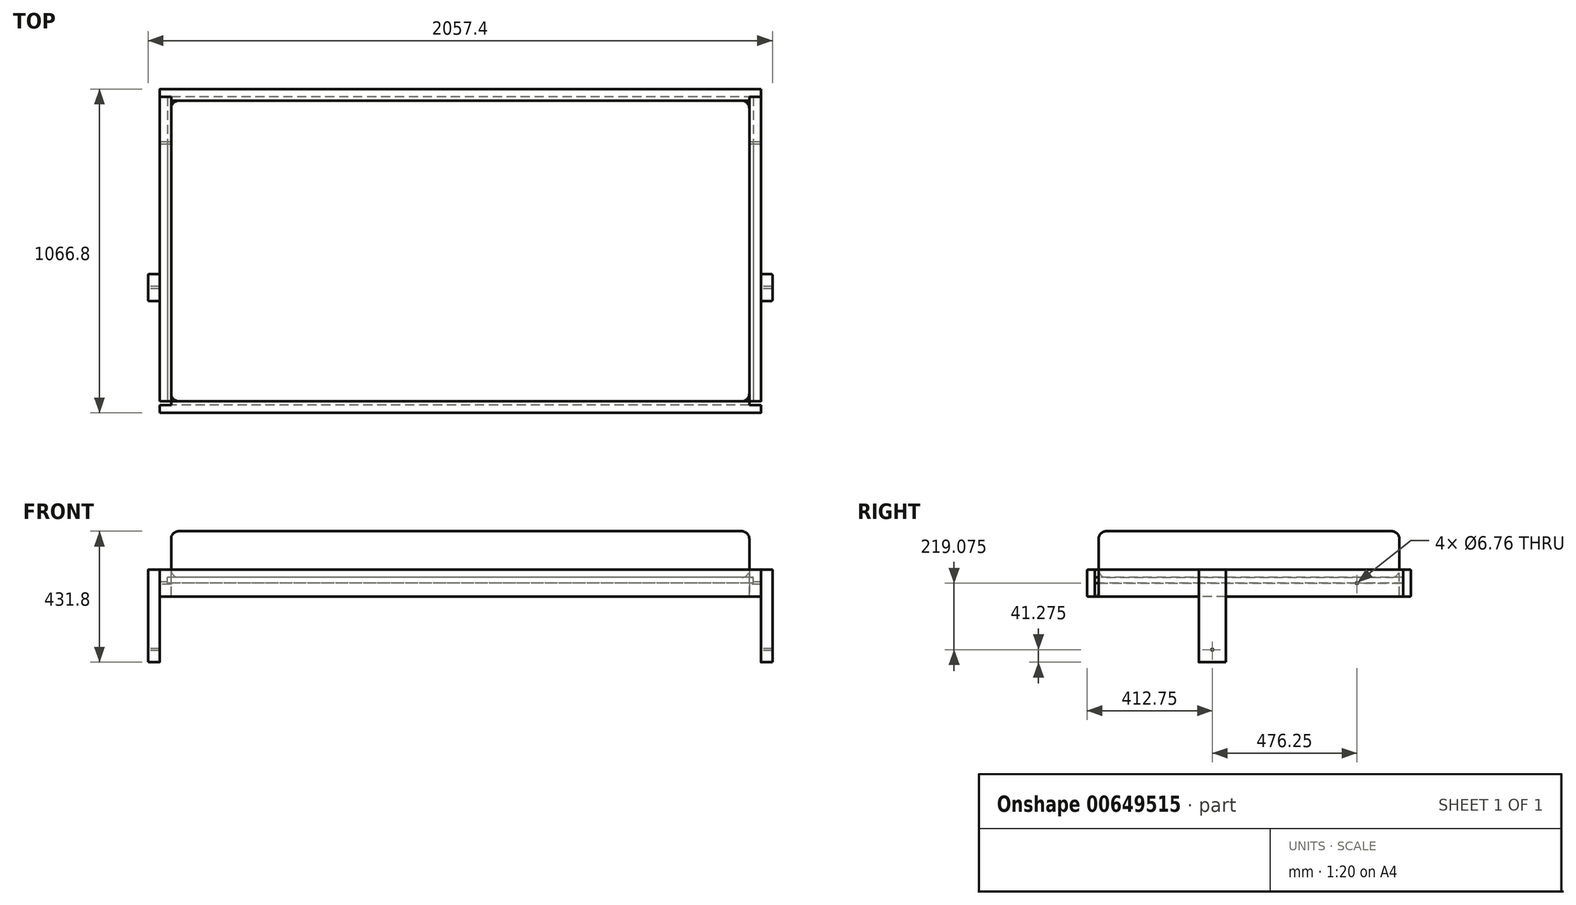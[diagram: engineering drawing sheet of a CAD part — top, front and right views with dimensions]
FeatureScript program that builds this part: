
annotation { "Feature Type Name" : "Feature", "Feature Type Description" : "" }
export const myFeature = defineFeature(function(context is Context, id is Id, definition is map)
    precondition{}
    {
        {
            var Q0;
            Q0=qCreatedBy(makeId("Top.planeOp"),FACE);
            var sketch = newSketch(context, id + "F0", { "sketchPlane" : qUnion([Q0])});
            skLineSegment(sketch, "E0.bottom", {"start": v(965.2, -508) * mm, "end": v(-965.2, -508) * mm});
            skLineSegment(sketch, "E0.top", {"start": v(965.2, 508) * mm, "end": v(-965.2, 508) * mm});
            skLineSegment(sketch, "E0.left", {"start": v(965.2, -508) * mm, "end": v(965.2, 508) * mm});
            skLineSegment(sketch, "E0.right", {"start": v(-965.2, -508) * mm, "end": v(-965.2, 508) * mm});
            skPoint(sketch, "E0.middle", {"position": v(0, 0) * mm});
            skLineSegment(sketch, "E1.0", {"start": v(952.5, 495.3) * mm, "end": v(-952.5, 495.3) * mm});
            skLineSegment(sketch, "E1.1", {"start": v(952.5, -495.3) * mm, "end": v(952.5, 495.3) * mm});
            skLineSegment(sketch, "E1.2", {"start": v(952.5, -495.3) * mm, "end": v(-952.5, -495.3) * mm});
            skLineSegment(sketch, "E1.3", {"start": v(-952.5, -495.3) * mm, "end": v(-952.5, 495.3) * mm});
            skLineSegment(sketch, "E2.0", {"start": v(990.6, 533.4) * mm, "end": v(-990.6, 533.4) * mm});
            skLineSegment(sketch, "E2.1", {"start": v(990.6, -533.4) * mm, "end": v(990.6, 533.4) * mm});
            skLineSegment(sketch, "E2.2", {"start": v(990.6, -533.4) * mm, "end": v(-990.6, -533.4) * mm});
            skLineSegment(sketch, "E2.3", {"start": v(-990.6, -533.4) * mm, "end": v(-990.6, 533.4) * mm});
            skSolve(sketch);
        }
        {
            var Q0;
            Q0=makeQuery(id+"F0.imprint","IMPRINT",FACE,{"disambiguationData":[TD([[makeQuery(id+"F0.imprint","IMPRINT",EDGE,{"derivedFrom":sQuery(id+"F0.wireOp",EDGE,"E1.0")}),1.0]])]});
            extrude(context, id + "F1", {"entities" : qUnion([Q0]), "depth" : 152.4 * mm, "offsetDistance" : 25.4 * mm});
        }
        {
            var Q0;
            Q0=makeQuery(id+"F1.opExtrude","CAP_FACE",FACE,{"disambiguationData":[OSD([sQuery(id+"F0.wireOp",EDGE,"E1.0"),sQuery(id+"F0.wireOp",EDGE,"E1.1"),sQuery(id+"F0.wireOp",EDGE,"E1.2"),sQuery(id+"F0.wireOp",EDGE,"E1.3")])],"isStart":false});
            var Q1;
            Q1=makeQuery(id+"F1.opExtrude","SWEPT_FACE",FACE,{"disambiguationData":[OSD([sQuery(id+"F0.wireOp",EDGE,"E1.3")])]});
            var Q2;
            Q2=makeQuery(id+"F1.opExtrude","SWEPT_FACE",FACE,{"disambiguationData":[OSD([sQuery(id+"F0.wireOp",EDGE,"E1.2")])]});
            var Q3;
            Q3=makeQuery(id+"F1.opExtrude","SWEPT_FACE",FACE,{"disambiguationData":[OSD([sQuery(id+"F0.wireOp",EDGE,"E1.1")])]});
            var Q4;
            Q4=makeQuery(id+"F1.opExtrude","SWEPT_FACE",FACE,{"disambiguationData":[OSD([sQuery(id+"F0.wireOp",EDGE,"E1.0")])]});
            fillet(context, id + "F2", {"entities" : qUnion([Q0, Q1, Q2, Q3, Q4]), "radius" : 25.4 * mm, "tangentPropagation" : true, "allowEdgeOverflow" : false});
        }
        {
            var Q0;
            Q0=makeQuery(id+"F0.imprint","IMPRINT",FACE,{"disambiguationData":[TD([[makeQuery(id+"F0.imprint","IMPRINT",EDGE,{"derivedFrom":sQuery(id+"F0.wireOp",EDGE,"E1.0")}),1.0]])]});
            var Q1;
            Q1=makeQuery(id+"F0.imprint","IMPRINT",FACE,{"disambiguationData":[TD([[makeQuery(id+"F0.imprint","IMPRINT",EDGE,{"derivedFrom":sQuery(id+"F0.wireOp",EDGE,"E0.bottom")}),-1.0]])]});
            extrude(context, id + "F3", {"entities" : qUnion([Q0, Q1]), "oppositeDirection" : true, "depth" : 19.05 * mm, "offsetDistance" : 25.4 * mm});
        }
        {
            var Q0;
            Q0=makeQuery(id+"F3.opExtrude","SWEPT_FACE",FACE,{"disambiguationData":[OSD([sQuery(id+"F0.wireOp",EDGE,"E0.bottom")])]});
            var sketch = newSketch(context, id + "F4", { "sketchPlane" : qUnion([Q0])});
            skLineSegment(sketch, "E3.bottom", {"start": v(-955.68, 25.4) * mm, "end": v(-987.43, 25.4) * mm});
            skLineSegment(sketch, "E3.top", {"start": v(-955.68, -63.5) * mm, "end": v(-987.43, -63.5) * mm});
            skLineSegment(sketch, "E3.left", {"start": v(-952.5, 22.23) * mm, "end": v(-952.5, -60.33) * mm});
            skLineSegment(sketch, "E3.right", {"start": v(-990.6, 22.23) * mm, "end": v(-990.6, -60.33) * mm});
            skPoint(sketch, "E3.middle", {"position": v(-971.55, -19.05) * mm});
            skPoint(sketch, "E4.visualSharp", {"position": v(-990.6, 25.4) * mm});
            skArc(sketch, "E4.filletArc", {"start": v(-987.43, 25.4) * mm, "mid": v(-989.67, 24.47) * mm, "end": v(-990.6, 22.23) * mm});
            skPoint(sketch, "E5.visualSharp", {"position": v(-952.5, 25.4) * mm});
            skArc(sketch, "E5.filletArc", {"start": v(-952.5, 22.23) * mm, "mid": v(-953.43, 24.47) * mm, "end": v(-955.68, 25.4) * mm});
            skPoint(sketch, "E6.visualSharp", {"position": v(-952.5, -63.5) * mm});
            skArc(sketch, "E6.filletArc", {"start": v(-955.68, -63.5) * mm, "mid": v(-953.43, -62.57) * mm, "end": v(-952.5, -60.33) * mm});
            skPoint(sketch, "E7.visualSharp", {"position": v(-990.6, -63.5) * mm});
            skArc(sketch, "E7.filletArc", {"start": v(-990.6, -60.33) * mm, "mid": v(-989.67, -62.57) * mm, "end": v(-987.43, -63.5) * mm});
            skSolve(sketch);
        }
        {
            var Q0;
            {var subQ5=sQuery(id+"F4.wireOp",EDGE,"E3.bottom");Q0=makeQuery(id+"F4.imprint","IMPRINT",FACE,{"disambiguationData":[TD([[makeQuery(id+"F4.imprint","IMPRINT",EDGE,{"derivedFrom":subQ5}),1.0]])]});}
            var Q1;
            Q1=makeQuery(id+"F3.opExtrude","SWEPT_FACE",FACE,{"disambiguationData":[OSD([sQuery(id+"F0.wireOp",EDGE,"E0.top")])]});
            extrude(context, id + "F5", {"entities" : qUnion([Q0]), "endBound" : BoundingType.UP_TO_SURFACE, "oppositeDirection" : true, "depth" : 25.4 * mm, "endBoundEntityFace" : qUnion([Q1]), "offsetDistance" : 25.4 * mm});
        }
        {
            var Q0;
            Q0=makeQuery(id+"F5.opExtrude","SWEPT_BODY",BODY,{"disambiguationData":[OSD([sQuery(id+"F0.wireOp",EDGE,"E0.bottom"),sQuery(id+"F0.wireOp",EDGE,"E0.right"),sQuery(id+"F4.wireOp",EDGE,"E3.bottom"),sQuery(id+"F4.wireOp",EDGE,"E3.top"),sQuery(id+"F4.wireOp",EDGE,"E3.left"),sQuery(id+"F4.wireOp",EDGE,"E3.right"),sQuery(id+"F4.wireOp",EDGE,"E4.filletArc"),sQuery(id+"F4.wireOp",EDGE,"E5.filletArc"),sQuery(id+"F4.wireOp",EDGE,"E6.filletArc"),sQuery(id+"F4.wireOp",EDGE,"E7.filletArc")])]});
            var Q1;
            Q1=qCreatedBy(makeId("Right.planeOp"),FACE);
            mirror(context, id + "F6", {"entities" : qUnion([Q0]), "mirrorPlane" : qUnion([Q1])});
        }
        {
            var Q0;
            Q0=makeQuery(id+"F5.opExtrude","SWEPT_FACE",FACE,{"disambiguationData":[OSD([sQuery(id+"F4.wireOp",EDGE,"E3.right")])]});
            var sketch = newSketch(context, id + "F7", { "sketchPlane" : qUnion([Q0])});
            skLineSegment(sketch, "E8.bottom", {"start": v(530.23, -63.5) * mm, "end": v(498.48, -63.5) * mm});
            skLineSegment(sketch, "E8.top", {"start": v(530.23, 25.4) * mm, "end": v(498.48, 25.4) * mm});
            skLineSegment(sketch, "E8.left", {"start": v(533.4, -60.33) * mm, "end": v(533.4, 22.22) * mm});
            skLineSegment(sketch, "E8.right", {"start": v(495.3, -60.33) * mm, "end": v(495.3, 22.22) * mm});
            skPoint(sketch, "E8.middle", {"position": v(514.35, -19.05) * mm});
            skPoint(sketch, "E9.visualSharp", {"position": v(495.3, 25.4) * mm});
            skArc(sketch, "E9.filletArc", {"start": v(498.48, 25.4) * mm, "mid": v(496.23, 24.47) * mm, "end": v(495.3, 22.22) * mm});
            skPoint(sketch, "E10.visualSharp", {"position": v(533.4, 25.4) * mm});
            skArc(sketch, "E10.filletArc", {"start": v(533.4, 22.22) * mm, "mid": v(532.47, 24.47) * mm, "end": v(530.23, 25.4) * mm});
            skPoint(sketch, "E11.visualSharp", {"position": v(533.4, -63.5) * mm});
            skArc(sketch, "E11.filletArc", {"start": v(530.23, -63.5) * mm, "mid": v(532.47, -62.57) * mm, "end": v(533.4, -60.33) * mm});
            skPoint(sketch, "E12.visualSharp", {"position": v(495.3, -63.5) * mm});
            skArc(sketch, "E12.filletArc", {"start": v(495.3, -60.33) * mm, "mid": v(496.23, -62.57) * mm, "end": v(498.48, -63.5) * mm});
            skSolve(sketch);
        }
        {
            var Q0;
            Q0 = qSketchRegion(id + "F7", true);
            var Q1;
            Q1=makeQuery(id+"F6.opPattern","COPY",FACE,{"derivedFrom":makeQuery(id+"F5.opExtrude","SWEPT_FACE",FACE,{"disambiguationData":[OSD([sQuery(id+"F4.wireOp",EDGE,"E3.right")])]}),"instanceName":"1"});
            extrude(context, id + "F8", {"entities" : qUnion([Q0]), "endBound" : BoundingType.UP_TO_SURFACE, "oppositeDirection" : true, "depth" : 25.4 * mm, "endBoundEntityFace" : qUnion([Q1]), "offsetDistance" : 25.4 * mm});
        }
        {
            var Q0;
            Q0=makeQuery(id+"F8.opExtrude","SWEPT_FACE",FACE,{"disambiguationData":[OSD([sQuery(id+"F7.wireOp",EDGE,"E8.top")])]});
            var sketch = newSketch(context, id + "F9", { "sketchPlane" : qUnion([Q0])});
            skLineSegment(sketch, "E13.0", {"start": v(-990.6, 508) * mm, "end": v(-990.6, -508) * mm});
            skLineSegment(sketch, "E13.2", {"start": v(-952.5, 508) * mm, "end": v(-952.5, -508) * mm});
            skLineSegment(sketch, "E14", {"start": v(-952.5, -508) * mm, "end": v(-990.6, -508) * mm});
            skLineSegment(sketch, "E15.0", {"start": v(990.6, -495.3) * mm, "end": v(-990.6, -495.3) * mm});
            skLineSegment(sketch, "E16.0", {"start": v(990.6, 508) * mm, "end": v(990.6, -508) * mm});
            skLineSegment(sketch, "E17.0", {"start": v(952.5, 508) * mm, "end": v(952.5, -508) * mm});
            skLineSegment(sketch, "E18", {"start": v(952.5, -508) * mm, "end": v(990.6, -508) * mm});
            skSolve(sketch);
        }
        {
            var Q0;
            Q0 = qSketchRegion(id + "F9", true);
            extrude(context, id + "F10", {"entities" : qUnion([Q0]), "operationType" : NewBodyOperationType.REMOVE, "endBound" : BoundingType.THROUGH_ALL, "oppositeDirection" : true, "depth" : 25.4 * mm, "offsetDistance" : 25.4 * mm});
        }
        {
            var Q0;
            Q0=makeQuery(id+"F8.opExtrude","SWEPT_BODY",BODY,{"disambiguationData":[OSD([sQuery(id+"F7.wireOp",EDGE,"E8.bottom"),sQuery(id+"F7.wireOp",EDGE,"E8.top"),sQuery(id+"F7.wireOp",EDGE,"E8.left"),sQuery(id+"F7.wireOp",EDGE,"E8.right"),sQuery(id+"F7.wireOp",EDGE,"E9.filletArc"),sQuery(id+"F7.wireOp",EDGE,"E10.filletArc"),sQuery(id+"F7.wireOp",EDGE,"E11.filletArc"),sQuery(id+"F7.wireOp",EDGE,"E12.filletArc")])]});
            var Q1;
            Q1=qCreatedBy(makeId("Front.planeOp"),FACE);
            mirror(context, id + "F11", {"entities" : qUnion([Q0]), "mirrorPlane" : qUnion([Q1])});
        }
        {
            var Q0;
            Q0=makeQuery(id+"F5.opExtrude","SWEPT_FACE",FACE,{"disambiguationData":[OSD([sQuery(id+"F4.wireOp",EDGE,"E3.bottom")])]});
            var sketch = newSketch(context, id + "F12", { "sketchPlane" : qUnion([Q0])});
            skLineSegment(sketch, "E19.bottom", {"start": v(-1025.53, -76.2) * mm, "end": v(-993.78, -76.2) * mm});
            skLineSegment(sketch, "E19.top", {"start": v(-1025.53, -165.1) * mm, "end": v(-993.78, -165.1) * mm});
            skLineSegment(sketch, "E19.left", {"start": v(-1028.7, -79.37) * mm, "end": v(-1028.7, -161.92) * mm});
            skLineSegment(sketch, "E19.right", {"start": v(-990.6, -79.37) * mm, "end": v(-990.6, -161.92) * mm});
            skPoint(sketch, "E19.middle", {"position": v(-1009.65, -120.65) * mm});
            skPoint(sketch, "E20.visualSharp", {"position": v(-1028.7, -76.2) * mm});
            skArc(sketch, "E20.filletArc", {"start": v(-1025.53, -76.2) * mm, "mid": v(-1027.77, -77.13) * mm, "end": v(-1028.7, -79.37) * mm});
            skPoint(sketch, "E21.visualSharp", {"position": v(-990.6, -76.2) * mm});
            skArc(sketch, "E21.filletArc", {"start": v(-990.6, -79.37) * mm, "mid": v(-991.53, -77.13) * mm, "end": v(-993.78, -76.2) * mm});
            skPoint(sketch, "E22.visualSharp", {"position": v(-990.6, -165.1) * mm});
            skArc(sketch, "E22.filletArc", {"start": v(-993.78, -165.1) * mm, "mid": v(-991.53, -164.17) * mm, "end": v(-990.6, -161.92) * mm});
            skPoint(sketch, "E23.visualSharp", {"position": v(-1028.7, -165.1) * mm});
            skArc(sketch, "E23.filletArc", {"start": v(-1028.7, -161.92) * mm, "mid": v(-1027.77, -164.17) * mm, "end": v(-1025.53, -165.1) * mm});
            skSolve(sketch);
        }
        {
            var Q0;
            Q0 = qSketchRegion(id + "F12", true);
            extrude(context, id + "F13", {"entities" : qUnion([Q0]), "oppositeDirection" : true, "depth" : 304.8 * mm, "offsetDistance" : 25.4 * mm});
        }
        {
            var Q0;
            Q0=makeQuery(id+"F13.opExtrude","SWEPT_FACE",FACE,{"disambiguationData":[OSD([sQuery(id+"F12.wireOp",EDGE,"E19.left")])]});
            var sketch = newSketch(context, id + "F14", { "sketchPlane" : qUnion([Q0])});
            skPoint(sketch, "E24", {"position": v(120.65, -238.12) * mm});
            skCircle(sketch, "E25", {"center": v(120.65, -238.12) * mm, "radius": 41.27 * mm, "construction": true});
            skSolve(sketch);
        }
        {
            var Q0;
            Q0=makeQuery(id+"F13.opExtrude","SWEPT_BODY",BODY,{"disambiguationData":[OSD([sQuery(id+"F12.wireOp",EDGE,"E19.bottom"),sQuery(id+"F12.wireOp",EDGE,"E19.top"),sQuery(id+"F12.wireOp",EDGE,"E19.left"),sQuery(id+"F12.wireOp",EDGE,"E19.right"),sQuery(id+"F12.wireOp",EDGE,"E20.filletArc"),sQuery(id+"F12.wireOp",EDGE,"E21.filletArc"),sQuery(id+"F12.wireOp",EDGE,"E22.filletArc"),sQuery(id+"F12.wireOp",EDGE,"E23.filletArc")])]});
            var Q1;
            Q1=qCreatedBy(makeId("Right.planeOp"),FACE);
            mirror(context, id + "F15", {"entities" : qUnion([Q0]), "mirrorPlane" : qUnion([Q1])});
        }
        {
            var Q0;
            Q0=makeQuery(id+"F5.opExtrude","SWEPT_FACE",FACE,{"disambiguationData":[OSD([sQuery(id+"F4.wireOp",EDGE,"E3.right")])]});
            var sketch = newSketch(context, id + "F16", { "sketchPlane" : qUnion([Q0])});
            skPoint(sketch, "E26", {"position": v(-355.6, -19.05) * mm});
            skCircle(sketch, "E27", {"center": v(-355.6, -19.05) * mm, "radius": 41.28 * mm});
            skSolve(sketch);
        }
        {
            var Q0;
            Q0=sQuery(id+"F14.wireOp",VERTEX,"E24");
            var Q1;
            Q1=sQuery(id+"F16.wireOp",VERTEX,"E26");
            var Q2;
            Q2=makeQuery(id+"F13.opExtrude","SWEPT_BODY",BODY,{"disambiguationData":[OSD([sQuery(id+"F12.wireOp",EDGE,"E19.bottom"),sQuery(id+"F12.wireOp",EDGE,"E19.top"),sQuery(id+"F12.wireOp",EDGE,"E19.left"),sQuery(id+"F12.wireOp",EDGE,"E19.right"),sQuery(id+"F12.wireOp",EDGE,"E20.filletArc"),sQuery(id+"F12.wireOp",EDGE,"E21.filletArc"),sQuery(id+"F12.wireOp",EDGE,"E22.filletArc"),sQuery(id+"F12.wireOp",EDGE,"E23.filletArc")])]});
            var Q3;
            Q3=makeQuery(id+"F5.opExtrude","SWEPT_BODY",BODY,{"disambiguationData":[OSD([sQuery(id+"F0.wireOp",EDGE,"E0.bottom"),sQuery(id+"F0.wireOp",EDGE,"E0.right"),sQuery(id+"F4.wireOp",EDGE,"E3.bottom"),sQuery(id+"F4.wireOp",EDGE,"E3.top"),sQuery(id+"F4.wireOp",EDGE,"E3.left"),sQuery(id+"F4.wireOp",EDGE,"E3.right"),sQuery(id+"F4.wireOp",EDGE,"E4.filletArc"),sQuery(id+"F4.wireOp",EDGE,"E5.filletArc"),sQuery(id+"F4.wireOp",EDGE,"E6.filletArc"),sQuery(id+"F4.wireOp",EDGE,"E7.filletArc")])]});
            var Q4;
            Q4=makeQuery(id+"F15.opPattern","COPY",BODY,{"derivedFrom":makeQuery(id+"F13.opExtrude","SWEPT_BODY",BODY,{"disambiguationData":[OSD([sQuery(id+"F12.wireOp",EDGE,"E19.bottom"),sQuery(id+"F12.wireOp",EDGE,"E19.top"),sQuery(id+"F12.wireOp",EDGE,"E19.left"),sQuery(id+"F12.wireOp",EDGE,"E19.right"),sQuery(id+"F12.wireOp",EDGE,"E20.filletArc"),sQuery(id+"F12.wireOp",EDGE,"E21.filletArc"),sQuery(id+"F12.wireOp",EDGE,"E22.filletArc"),sQuery(id+"F12.wireOp",EDGE,"E23.filletArc")])]}),"instanceName":"1"});
            var Q5;
            Q5=makeQuery(id+"F6.opPattern","COPY",BODY,{"derivedFrom":makeQuery(id+"F5.opExtrude","SWEPT_BODY",BODY,{"disambiguationData":[OSD([sQuery(id+"F0.wireOp",EDGE,"E0.bottom"),sQuery(id+"F0.wireOp",EDGE,"E0.right"),sQuery(id+"F4.wireOp",EDGE,"E3.bottom"),sQuery(id+"F4.wireOp",EDGE,"E3.top"),sQuery(id+"F4.wireOp",EDGE,"E3.left"),sQuery(id+"F4.wireOp",EDGE,"E3.right"),sQuery(id+"F4.wireOp",EDGE,"E4.filletArc"),sQuery(id+"F4.wireOp",EDGE,"E5.filletArc"),sQuery(id+"F4.wireOp",EDGE,"E6.filletArc"),sQuery(id+"F4.wireOp",EDGE,"E7.filletArc")])]}),"instanceName":"1"});
            hole(context, id + "F17", {"style" : HoleStyle.SIMPLE, "endStyle" : HoleEndStyle.THROUGH, "standardTappedOrClearance" : lookupTablePath({ "standard" : "ANSI", "fit" : "Normal (ASME)", "size" : "1/4", "type" : "Clearance" }), "standardBlindInLast" : lookupTablePath({ "fit" : "Free", "standard" : "ANSI", "size" : "1/4", "type" : "Clearance" }), "holeDiameter" : 6.76 * mm, "majorDiameter" : 6.35 * mm, "isTappedThrough" : true, "tappedDepth" : 12.7 * mm, "tapClearance" : 3, "locations" : qUnion([Q0, Q1]), "scope" : qUnion([Q2, Q3, Q4, Q5])});
        }
    });
